# Revit family: Magnuson-Frame-Coat_Rack-1
name_source: partatom
category: Furniture
revit_build: Autodesk Revit 2016 (Build: 20150220_1215(x64)
units: mm (PartAtom-declared; Revit-internal decimal feet)

## family parameters
Always vertical = Yes
Cut with Voids When Loaded = No
OmniClass Number = 23.40.20.00
OmniClass Title = General Furniture and Specialties
Room Calculation Point = No
Shared = No
Work Plane-Based = No

## types (1)
- Type Catalog
    Assembly Code = E2020200
    Depth = 17 21/32"
    Description = Type Catalog
    Frame Finish = MAG-Powder_Coat-Black
    Glide Finish = MAG-Plastic-Black
    Height = 67 3/32"
    Interior Panel Finish = MAG-Wood-Black
    Keynote = 12500
    Low Emitting Finish = Yes
    Low Emitting Material = Yes
    Manufacturer = Magnuson Group
    Model = Type Catalog
    Out Panel Finish = MAG-Cork-Linoleum
    Panel = Yes
    Percentage of Recycled Content = 0
    Salvage or Reuse = Yes
    Type Comments = FRAME
    URL = www.magnusongroup.com
    Width = 18 1/2"

## geometry (parser evidence)
native form markers: Sweep x1
no freeform markers — native parametric forms only
